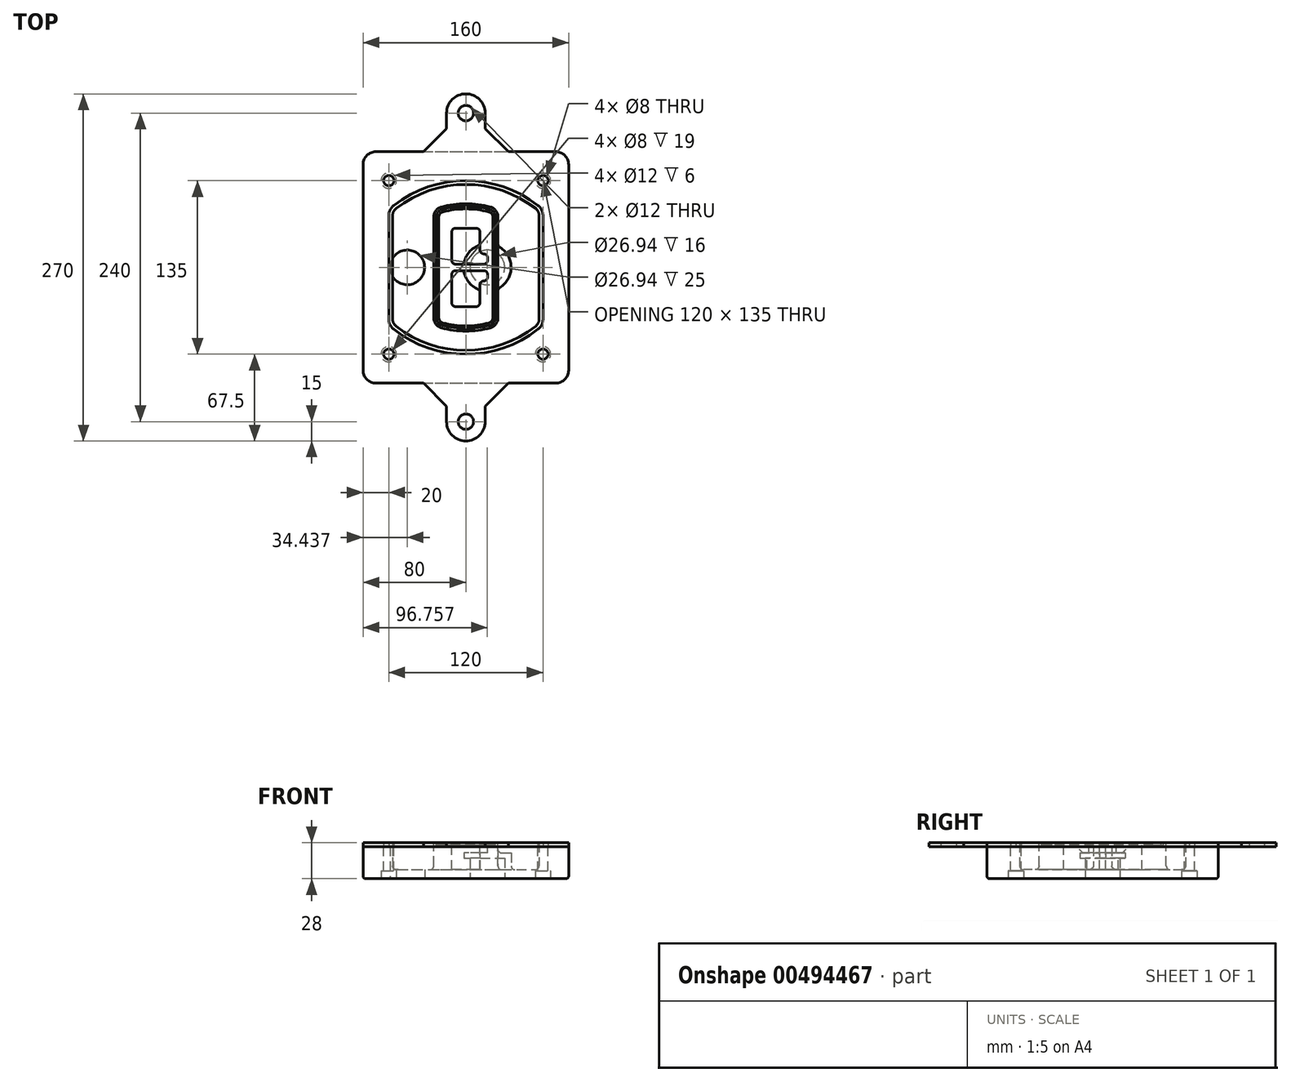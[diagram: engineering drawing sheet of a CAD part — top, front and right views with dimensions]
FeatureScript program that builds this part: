
annotation { "Feature Type Name" : "Feature", "Feature Type Description" : "" }
export const myFeature = defineFeature(function(context is Context, id is Id, definition is map)
    precondition{}
    {
        {
            var Q0;
            Q0=qCreatedBy(makeId("Top.planeOp"),FACE);
            var sketch = newSketch(context, id + "F0", { "sketchPlane" : qUnion([Q0])});
            skPoint(sketch, "E0.rect.middle", {"position": v(0, 0) * mm});
            skLineSegment(sketch, "E1.bottom", {"start": v(-70, -90) * mm, "end": v(70, -90) * mm});
            skLineSegment(sketch, "E1.top", {"start": v(-70, 90) * mm, "end": v(70, 90) * mm});
            skLineSegment(sketch, "E1.left", {"start": v(-80, -80) * mm, "end": v(-80, 80) * mm});
            skLineSegment(sketch, "E1.right", {"start": v(80, -80) * mm, "end": v(80, 80) * mm});
            skLineSegment(sketch, "E2", {"start": v(-80, 90) * mm, "end": v(80, -90) * mm, "construction": true});
            skLineSegment(sketch, "E3", {"start": v(80, 90) * mm, "end": v(-80, -90) * mm, "construction": true});
            skCircle(sketch, "E4", {"center": v(-60, 67.5) * mm, "radius": 4 * mm});
            skCircle(sketch, "E5", {"center": v(60, 67.5) * mm, "radius": 4 * mm});
            skCircle(sketch, "E6", {"center": v(60, -67.5) * mm, "radius": 4 * mm});
            skCircle(sketch, "E7", {"center": v(-60, -67.5) * mm, "radius": 4 * mm});
            skLineSegment(sketch, "E8", {"start": v(-60, 67.5) * mm, "end": v(60, 67.5) * mm, "construction": true});
            skLineSegment(sketch, "E9", {"start": v(60, 67.5) * mm, "end": v(60, -67.5) * mm, "construction": true});
            skLineSegment(sketch, "E10", {"start": v(60, -67.5) * mm, "end": v(-60, -67.5) * mm, "construction": true});
            skLineSegment(sketch, "E11", {"start": v(-60, -67.5) * mm, "end": v(-60, 67.5) * mm, "construction": true});
            skLineSegment(sketch, "E12", {"start": v(-60, 40.3) * mm, "end": v(-60, -40.3) * mm});
            skLineSegment(sketch, "E13", {"start": v(60, 40.3) * mm, "end": v(60, -40.3) * mm});
            skArc(sketch, "E14", {"start": v(56.15, 48.18) * mm, "mid": v(0, 67.5) * mm, "end": v(-56.15, 48.18) * mm});
            skArc(sketch, "E15", {"start": v(-56.15, -48.18) * mm, "mid": v(0, -67.5) * mm, "end": v(56.15, -48.18) * mm});
            skLineSegment(sketch, "E16", {"start": v(-60, 0) * mm, "end": v(60, 0) * mm, "construction": true});
            skPoint(sketch, "E17.visualSharp", {"position": v(-60, -45) * mm});
            skArc(sketch, "E17.filletArc", {"start": v(-60, -40.3) * mm, "mid": v(-58.99, -44.68) * mm, "end": v(-56.15, -48.18) * mm});
            skPoint(sketch, "E18.visualSharp", {"position": v(-60, 45) * mm});
            skArc(sketch, "E18.filletArc", {"start": v(-56.15, 48.18) * mm, "mid": v(-58.99, 44.68) * mm, "end": v(-60, 40.3) * mm});
            skPoint(sketch, "E19.visualSharp", {"position": v(60, 45) * mm});
            skArc(sketch, "E19.filletArc", {"start": v(60, 40.3) * mm, "mid": v(58.99, 44.68) * mm, "end": v(56.15, 48.18) * mm});
            skPoint(sketch, "E20.visualSharp", {"position": v(60, -45) * mm});
            skArc(sketch, "E20.filletArc", {"start": v(56.15, -48.18) * mm, "mid": v(58.99, -44.68) * mm, "end": v(60, -40.3) * mm});
            skPoint(sketch, "E21.visualSharp", {"position": v(-80, 90) * mm});
            skArc(sketch, "E21.filletArc", {"start": v(-70, 90) * mm, "mid": v(-77.07, 87.07) * mm, "end": v(-80, 80) * mm});
            skPoint(sketch, "E22.visualSharp", {"position": v(80, 90) * mm});
            skArc(sketch, "E22.filletArc", {"start": v(80, 80) * mm, "mid": v(77.07, 87.07) * mm, "end": v(70, 90) * mm});
            skPoint(sketch, "E23.visualSharp", {"position": v(80, -90) * mm});
            skArc(sketch, "E23.filletArc", {"start": v(70, -90) * mm, "mid": v(77.07, -87.07) * mm, "end": v(80, -80) * mm});
            skPoint(sketch, "E24.visualSharp", {"position": v(-80, -90) * mm});
            skArc(sketch, "E24.filletArc", {"start": v(-80, -80) * mm, "mid": v(-77.07, -87.07) * mm, "end": v(-70, -90) * mm});
            skArc(sketch, "E25.0", {"start": v(57, 40.3) * mm, "mid": v(56.3, 43.36) * mm, "end": v(54.3, 45.81) * mm});
            skLineSegment(sketch, "E25.1", {"start": v(57, 40.3) * mm, "end": v(57, -40.3) * mm});
            skArc(sketch, "E25.2", {"start": v(54.3, -45.81) * mm, "mid": v(56.3, -43.36) * mm, "end": v(57, -40.3) * mm});
            skArc(sketch, "E25.3", {"start": v(-54.3, -45.81) * mm, "mid": v(0, -64.5) * mm, "end": v(54.3, -45.81) * mm});
            skArc(sketch, "E25.4", {"start": v(-57, -40.3) * mm, "mid": v(-56.3, -43.36) * mm, "end": v(-54.3, -45.81) * mm});
            skArc(sketch, "E25.5", {"start": v(54.3, 45.81) * mm, "mid": v(0, 64.5) * mm, "end": v(-54.3, 45.81) * mm});
            skLineSegment(sketch, "E25.6", {"start": v(-57, 40.3) * mm, "end": v(-57, -40.3) * mm});
            skArc(sketch, "E25.7", {"start": v(-54.3, 45.81) * mm, "mid": v(-56.3, 43.36) * mm, "end": v(-57, 40.3) * mm});
            skArc(sketch, "E26.0", {"start": v(-58.62, 51.33) * mm, "mid": v(-62.58, 46.43) * mm, "end": v(-64, 40.3) * mm});
            skArc(sketch, "E26.1", {"start": v(58.62, 51.33) * mm, "mid": v(0, 71.5) * mm, "end": v(-58.62, 51.33) * mm});
            skArc(sketch, "E26.2", {"start": v(64, 40.3) * mm, "mid": v(62.58, 46.43) * mm, "end": v(58.62, 51.33) * mm});
            skLineSegment(sketch, "E26.3", {"start": v(64, 40.3) * mm, "end": v(64, -40.3) * mm});
            skArc(sketch, "E26.4", {"start": v(58.62, -51.33) * mm, "mid": v(62.58, -46.43) * mm, "end": v(64, -40.3) * mm});
            skLineSegment(sketch, "E26.5", {"start": v(-64, 40.3) * mm, "end": v(-64, -40.3) * mm});
            skArc(sketch, "E26.6", {"start": v(-58.62, -51.33) * mm, "mid": v(0, -71.5) * mm, "end": v(58.62, -51.33) * mm});
            skArc(sketch, "E26.7", {"start": v(-64, -40.3) * mm, "mid": v(-62.58, -46.43) * mm, "end": v(-58.62, -51.33) * mm});
            skSolve(sketch);
        }
        {
            var Q0;
            Q0=makeQuery(id+"F0.imprint","IMPRINT",FACE,{"disambiguationData":[TD([[makeQuery(id+"F0.imprint","IMPRINT",EDGE,{"derivedFrom":sQuery(id+"F0.wireOp",EDGE,"E1.bottom")}),1.0]])]});
            var Q1;
            Q1=makeQuery(id+"F0.imprint","IMPRINT",FACE,{"disambiguationData":[TD([[makeQuery(id+"F0.imprint","IMPRINT",EDGE,{"derivedFrom":sQuery(id+"F0.wireOp",EDGE,"E12")}),1.0]])]});
            var Q2;
            Q2=makeQuery(id+"F0.imprint","IMPRINT",FACE,{"disambiguationData":[TD([[makeQuery(id+"F0.imprint","IMPRINT",EDGE,{"derivedFrom":sQuery(id+"F0.wireOp",EDGE,"E25.0")}),1.0]])]});
            var Q3;
            Q3=makeQuery(id+"F0.imprint","IMPRINT",FACE,{"disambiguationData":[TD([[makeQuery(id+"F0.imprint","IMPRINT",EDGE,{"derivedFrom":sQuery(id+"F0.wireOp",EDGE,"E12")}),-1.0]])]});
            extrude(context, id + "F1", {"entities" : qUnion([Q0, Q1, Q2, Q3]), "oppositeDirection" : true, "depth" : 25 * mm});
        }
        {
            var Q0;
            Q0=makeQuery(id+"F0.imprint","IMPRINT",FACE,{"disambiguationData":[TD([[makeQuery(id+"F0.imprint","IMPRINT",EDGE,{"derivedFrom":sQuery(id+"F0.wireOp",EDGE,"E12")}),1.0]])]});
            extrude(context, id + "F2", {"entities" : qUnion([Q0]), "operationType" : NewBodyOperationType.ADD, "depth" : 3 * mm});
        }
        {
            var Q0;
            Q0=makeQuery(id+"F0.imprint","IMPRINT",FACE,{"disambiguationData":[TD([[makeQuery(id+"F0.imprint","IMPRINT",EDGE,{"derivedFrom":sQuery(id+"F0.wireOp",EDGE,"E25.0")}),1.0]])]});
            extrude(context, id + "F3", {"entities" : qUnion([Q0]), "operationType" : NewBodyOperationType.REMOVE, "oppositeDirection" : true, "depth" : 18 * mm});
        }
        {
            var Q0;
            Q0=makeQuery(id+"F2.opExtrude","CAP_FACE",FACE,{"disambiguationData":[OSD([sQuery(id+"F0.wireOp",EDGE,"E12"),sQuery(id+"F0.wireOp",EDGE,"E13"),sQuery(id+"F0.wireOp",EDGE,"E14"),sQuery(id+"F0.wireOp",EDGE,"E15"),sQuery(id+"F0.wireOp",EDGE,"E17.filletArc"),sQuery(id+"F0.wireOp",EDGE,"E18.filletArc"),sQuery(id+"F0.wireOp",EDGE,"E19.filletArc"),sQuery(id+"F0.wireOp",EDGE,"E20.filletArc"),sQuery(id+"F0.wireOp",EDGE,"E25.0"),sQuery(id+"F0.wireOp",EDGE,"E25.1"),sQuery(id+"F0.wireOp",EDGE,"E25.2"),sQuery(id+"F0.wireOp",EDGE,"E25.3"),sQuery(id+"F0.wireOp",EDGE,"E25.4"),sQuery(id+"F0.wireOp",EDGE,"E25.5"),sQuery(id+"F0.wireOp",EDGE,"E25.6"),sQuery(id+"F0.wireOp",EDGE,"E25.7")])],"isStart":false});
            var sketch = newSketch(context, id + "F4", { "sketchPlane" : qUnion([Q0])});
            skArc(sketch, "E27.0", {"start": v(-19.08, -46.97) * mm, "mid": v(0, -49.5) * mm, "end": v(19.08, -46.97) * mm});
            skArc(sketch, "E28.0", {"start": v(19.08, 46.97) * mm, "mid": v(0, 49.5) * mm, "end": v(-19.08, 46.97) * mm});
            skLineSegment(sketch, "E29", {"start": v(-25, 39.25) * mm, "end": v(-25, -39.25) * mm});
            skLineSegment(sketch, "E30", {"start": v(25, 39.25) * mm, "end": v(25, -39.25) * mm});
            skLineSegment(sketch, "E31", {"start": v(-25, 45.1) * mm, "end": v(25, 45.1) * mm, "construction": true});
            skLineSegment(sketch, "E32", {"start": v(-25, -45.1) * mm, "end": v(25, -45.1) * mm, "construction": true});
            skPoint(sketch, "E33.visualSharp", {"position": v(-25, 45.1) * mm});
            skArc(sketch, "E33.filletArc", {"start": v(-19.08, 46.97) * mm, "mid": v(-23.35, 44.11) * mm, "end": v(-25, 39.25) * mm});
            skPoint(sketch, "E34.visualSharp", {"position": v(25, 45.1) * mm});
            skArc(sketch, "E34.filletArc", {"start": v(25, 39.25) * mm, "mid": v(23.35, 44.11) * mm, "end": v(19.08, 46.97) * mm});
            skPoint(sketch, "E35.visualSharp", {"position": v(25, -45.1) * mm});
            skArc(sketch, "E35.filletArc", {"start": v(19.08, -46.97) * mm, "mid": v(23.35, -44.11) * mm, "end": v(25, -39.25) * mm});
            skPoint(sketch, "E36.visualSharp", {"position": v(-25, -45.1) * mm});
            skArc(sketch, "E36.filletArc", {"start": v(-25, -39.25) * mm, "mid": v(-23.35, -44.11) * mm, "end": v(-19.08, -46.97) * mm});
            skArc(sketch, "E37.0", {"start": v(54.3, 45.81) * mm, "mid": v(0, 64.5) * mm, "end": v(-54.3, 45.81) * mm});
            skArc(sketch, "E37.1", {"start": v(-54.3, 45.81) * mm, "mid": v(-56.3, 43.36) * mm, "end": v(-57, 40.3) * mm});
            skLineSegment(sketch, "E37.2", {"start": v(-57, 40.3) * mm, "end": v(-57, -40.3) * mm});
            skArc(sketch, "E37.3", {"start": v(-57, -40.3) * mm, "mid": v(-56.3, -43.36) * mm, "end": v(-54.3, -45.81) * mm});
            skArc(sketch, "E37.4", {"start": v(-54.3, -45.81) * mm, "mid": v(0, -64.5) * mm, "end": v(54.3, -45.81) * mm});
            skArc(sketch, "E37.5", {"start": v(54.3, -45.81) * mm, "mid": v(56.3, -43.36) * mm, "end": v(57, -40.3) * mm});
            skLineSegment(sketch, "E37.6", {"start": v(57, 40.3) * mm, "end": v(57, -40.3) * mm});
            skArc(sketch, "E37.7", {"start": v(57, 40.3) * mm, "mid": v(56.3, 43.36) * mm, "end": v(54.3, 45.81) * mm});
            skLineSegment(sketch, "E38.0", {"start": v(23, 39.25) * mm, "end": v(23, -39.25) * mm});
            skArc(sketch, "E38.1", {"start": v(18.56, -45.04) * mm, "mid": v(21.76, -42.9) * mm, "end": v(23, -39.25) * mm});
            skArc(sketch, "E38.2", {"start": v(-18.56, -45.04) * mm, "mid": v(0, -47.5) * mm, "end": v(18.56, -45.04) * mm});
            skArc(sketch, "E38.3", {"start": v(-23, -39.25) * mm, "mid": v(-21.76, -42.9) * mm, "end": v(-18.56, -45.04) * mm});
            skLineSegment(sketch, "E38.4", {"start": v(-23, 39.25) * mm, "end": v(-23, -39.25) * mm});
            skArc(sketch, "E38.5", {"start": v(23, 39.25) * mm, "mid": v(21.76, 42.9) * mm, "end": v(18.56, 45.04) * mm});
            skArc(sketch, "E38.6", {"start": v(-18.56, 45.04) * mm, "mid": v(-21.76, 42.9) * mm, "end": v(-23, 39.25) * mm});
            skArc(sketch, "E38.7", {"start": v(18.56, 45.04) * mm, "mid": v(0, 47.5) * mm, "end": v(-18.56, 45.04) * mm});
            skArc(sketch, "E39.0", {"start": v(21, 39.25) * mm, "mid": v(20.18, 41.68) * mm, "end": v(18.04, 43.1) * mm});
            skLineSegment(sketch, "E39.1", {"start": v(21, 39.25) * mm, "end": v(21, -39.25) * mm});
            skArc(sketch, "E39.2", {"start": v(18.04, -43.1) * mm, "mid": v(20.18, -41.68) * mm, "end": v(21, -39.25) * mm});
            skArc(sketch, "E39.3", {"start": v(-18.04, -43.1) * mm, "mid": v(0, -45.5) * mm, "end": v(18.04, -43.1) * mm});
            skArc(sketch, "E39.4", {"start": v(-21, -39.25) * mm, "mid": v(-20.18, -41.68) * mm, "end": v(-18.04, -43.1) * mm});
            skArc(sketch, "E39.5", {"start": v(18.04, 43.1) * mm, "mid": v(0, 45.5) * mm, "end": v(-18.04, 43.1) * mm});
            skLineSegment(sketch, "E39.6", {"start": v(-21, 39.25) * mm, "end": v(-21, -39.25) * mm});
            skArc(sketch, "E39.7", {"start": v(-18.04, 43.1) * mm, "mid": v(-20.18, 41.68) * mm, "end": v(-21, 39.25) * mm});
            skLineSegment(sketch, "E40", {"start": v(-25, 0) * mm, "end": v(25, 0) * mm, "construction": true});
            skLineSegment(sketch, "E41", {"start": v(-11, 5.5) * mm, "end": v(-11, 27.5) * mm});
            skLineSegment(sketch, "E42", {"start": v(-8, 30.5) * mm, "end": v(8, 30.5) * mm});
            skLineSegment(sketch, "E43", {"start": v(11, 27.5) * mm, "end": v(11, 13.5) * mm});
            skLineSegment(sketch, "E44", {"start": v(14, 10.5) * mm, "end": v(14, 10.5) * mm});
            skLineSegment(sketch, "E45", {"start": v(17, 7.5) * mm, "end": v(17, 5.5) * mm});
            skLineSegment(sketch, "E46", {"start": v(14, 2.5) * mm, "end": v(-8, 2.5) * mm});
            skPoint(sketch, "E47.visualSharp", {"position": v(-11, 30.5) * mm});
            skArc(sketch, "E47.filletArc", {"start": v(-8, 30.5) * mm, "mid": v(-10.12, 29.62) * mm, "end": v(-11, 27.5) * mm});
            skPoint(sketch, "E48.visualSharp", {"position": v(11, 30.5) * mm});
            skArc(sketch, "E48.filletArc", {"start": v(11, 27.5) * mm, "mid": v(10.12, 29.62) * mm, "end": v(8, 30.5) * mm});
            skPoint(sketch, "E49.visualSharp", {"position": v(11, 10.5) * mm});
            skArc(sketch, "E49.filletArc", {"start": v(11, 13.5) * mm, "mid": v(11.88, 11.38) * mm, "end": v(14, 10.5) * mm});
            skPoint(sketch, "E50.visualSharp", {"position": v(17, 10.5) * mm});
            skArc(sketch, "E50.filletArc", {"start": v(17, 7.5) * mm, "mid": v(16.12, 9.62) * mm, "end": v(14, 10.5) * mm});
            skPoint(sketch, "E51.visualSharp", {"position": v(17, 2.5) * mm});
            skArc(sketch, "E51.filletArc", {"start": v(14, 2.5) * mm, "mid": v(16.12, 3.38) * mm, "end": v(17, 5.5) * mm});
            skPoint(sketch, "E52.visualSharp", {"position": v(-11, 2.5) * mm});
            skArc(sketch, "E52.filletArc", {"start": v(-11, 5.5) * mm, "mid": v(-10.12, 3.38) * mm, "end": v(-8, 2.5) * mm});
            skLineSegment(sketch, "E53.0.MirrorCS", {"start": v(14, -2.5) * mm, "end": v(-8, -2.5) * mm});
            skArc(sketch, "E54.0.MirrorCS", {"start": v(-11, -5.5) * mm, "mid": v(-10.12, -3.38) * mm, "end": v(-8, -2.5) * mm});
            skLineSegment(sketch, "E55.0.MirrorCS", {"start": v(-11, -5.5) * mm, "end": v(-11, -27.5) * mm});
            skArc(sketch, "E56.0.MirrorCS", {"start": v(-8, -30.5) * mm, "mid": v(-10.12, -29.62) * mm, "end": v(-11, -27.5) * mm});
            skLineSegment(sketch, "E57.0.MirrorCS", {"start": v(-8, -30.5) * mm, "end": v(8, -30.5) * mm});
            skArc(sketch, "E58.0.MirrorCS", {"start": v(11, -27.5) * mm, "mid": v(10.12, -29.62) * mm, "end": v(8, -30.5) * mm});
            skLineSegment(sketch, "E59.0.MirrorCS", {"start": v(11, -27.5) * mm, "end": v(11, -13.5) * mm});
            skArc(sketch, "E60.0.MirrorCS", {"start": v(11, -13.5) * mm, "mid": v(11.88, -11.38) * mm, "end": v(14, -10.5) * mm});
            skArc(sketch, "E61.0.MirrorCS", {"start": v(17, -7.5) * mm, "mid": v(16.12, -9.62) * mm, "end": v(14, -10.5) * mm});
            skLineSegment(sketch, "E62.0.MirrorCS", {"start": v(17, -7.5) * mm, "end": v(17, -5.5) * mm});
            skArc(sketch, "E63.0.MirrorCS", {"start": v(14, -2.5) * mm, "mid": v(16.12, -3.38) * mm, "end": v(17, -5.5) * mm});
            skSolve(sketch);
        }
        {
            var Q0;
            Q0=makeQuery(id+"F4.imprint","IMPRINT",FACE,{"disambiguationData":[TD([[makeQuery(id+"F4.imprint","IMPRINT",EDGE,{"derivedFrom":sQuery(id+"F4.wireOp",EDGE,"E27.0")}),1.0]])]});
            var Q1;
            Q1=makeQuery(id+"F4.imprint","IMPRINT",FACE,{"disambiguationData":[TD([[makeQuery(id+"F4.imprint","IMPRINT",EDGE,{"derivedFrom":sQuery(id+"F4.wireOp",EDGE,"E38.0")}),-1.0]])]});
            var Q2;
            Q2=makeQuery(id+"F4.imprint","IMPRINT",FACE,{"disambiguationData":[TD([[makeQuery(id+"F4.imprint","IMPRINT",EDGE,{"derivedFrom":sQuery(id+"F4.wireOp",EDGE,"E39.0")}),1.0]])]});
            extrude(context, id + "F5", {"entities" : qUnion([Q0, Q1, Q2]), "operationType" : NewBodyOperationType.ADD, "endBound" : BoundingType.UP_TO_NEXT, "oppositeDirection" : true, "depth" : 25 * mm});
        }
        {
            var Q0;
            Q0=makeQuery(id+"F4.imprint","IMPRINT",FACE,{"disambiguationData":[TD([[makeQuery(id+"F4.imprint","IMPRINT",EDGE,{"derivedFrom":sQuery(id+"F4.wireOp",EDGE,"E38.0")}),-1.0]])]});
            extrude(context, id + "F6", {"entities" : qUnion([Q0]), "operationType" : NewBodyOperationType.REMOVE, "oppositeDirection" : true, "depth" : 2 * mm});
        }
        {
            var Q0;
            Q0=makeQuery(id+"F1.opExtrude","CAP_FACE",FACE,{"disambiguationData":[OSD([sQuery(id+"F0.wireOp",EDGE,"E1.bottom"),sQuery(id+"F0.wireOp",EDGE,"E1.top"),sQuery(id+"F0.wireOp",EDGE,"E1.left"),sQuery(id+"F0.wireOp",EDGE,"E1.right"),sQuery(id+"F0.wireOp",EDGE,"E4"),sQuery(id+"F0.wireOp",EDGE,"E5"),sQuery(id+"F0.wireOp",EDGE,"E6"),sQuery(id+"F0.wireOp",EDGE,"E7"),sQuery(id+"F0.wireOp",EDGE,"E21.filletArc"),sQuery(id+"F0.wireOp",EDGE,"E22.filletArc"),sQuery(id+"F0.wireOp",EDGE,"E23.filletArc"),sQuery(id+"F0.wireOp",EDGE,"E24.filletArc")])],"isStart":false});
            var sketch = newSketch(context, id + "F7", { "sketchPlane" : qUnion([Q0])});
            skCircle(sketch, "E64", {"center": v(16.76, 0) * mm, "radius": 13.47 * mm});
            skCircle(sketch, "E65", {"center": v(-45.56, 0) * mm, "radius": 13.47 * mm});
            skLineSegment(sketch, "E66", {"start": v(80, 0) * mm, "end": v(-80, 0) * mm});
            skCircle(sketch, "E67", {"center": v(16.76, 0) * mm, "radius": 18.47 * mm});
            skCircle(sketch, "E68", {"center": v(60, -67.5) * mm, "radius": 6 * mm});
            skCircle(sketch, "E69", {"center": v(-60, -67.5) * mm, "radius": 6 * mm});
            skCircle(sketch, "E70", {"center": v(-60, 67.5) * mm, "radius": 6 * mm});
            skCircle(sketch, "E71", {"center": v(60, 67.5) * mm, "radius": 6 * mm});
            skSolve(sketch);
        }
        {
            var Q0;
            {var subQ1=sQuery(id+"F7.wireOp",EDGE,"E66");var subQ4=sQuery(id+"F7.wireOp",EDGE,"E64");var subQ6=makeQuery(id+"F7.imprint","INTERSECT",VERTEX,{"disambiguationData":[OD(0.0)],"derivedFrom":[subQ4,subQ1]});Q0=makeQuery(id+"F7.imprint","IMPRINT",FACE,{"disambiguationData":[TD([[makeQuery(id+"F7.imprint","IMPRINT",EDGE,{"disambiguationData":[TD([[subQ6,-1.0]])],"derivedFrom":subQ4}),-1.0]])]});}
            var Q1;
            {var subQ0=sQuery(id+"F7.wireOp",EDGE,"E66");var subQ1=sQuery(id+"F7.wireOp",EDGE,"E64");var subQ3=makeQuery(id+"F7.imprint","INTERSECT",VERTEX,{"disambiguationData":[OD(0.0)],"derivedFrom":[subQ1,subQ0]});Q1=makeQuery(id+"F7.imprint","IMPRINT",FACE,{"disambiguationData":[TD([[makeQuery(id+"F7.imprint","IMPRINT",EDGE,{"disambiguationData":[TD([[subQ3,-1.0]])],"derivedFrom":subQ1}),1.0]])]});}
            var Q2;
            {var subQ0=sQuery(id+"F7.wireOp",EDGE,"E66");var subQ1=sQuery(id+"F7.wireOp",EDGE,"E64");var subQ3=makeQuery(id+"F7.imprint","INTERSECT",VERTEX,{"disambiguationData":[OD(0.0)],"derivedFrom":[subQ1,subQ0]});Q2=makeQuery(id+"F7.imprint","IMPRINT",FACE,{"disambiguationData":[TD([[makeQuery(id+"F7.imprint","IMPRINT",EDGE,{"disambiguationData":[TD([[subQ3,1.0]])],"derivedFrom":subQ1}),1.0]])]});}
            var Q3;
            {var subQ1=sQuery(id+"F7.wireOp",EDGE,"E66");var subQ4=sQuery(id+"F7.wireOp",EDGE,"E64");var subQ6=makeQuery(id+"F7.imprint","INTERSECT",VERTEX,{"disambiguationData":[OD(0.0)],"derivedFrom":[subQ4,subQ1]});Q3=makeQuery(id+"F7.imprint","IMPRINT",FACE,{"disambiguationData":[TD([[makeQuery(id+"F7.imprint","IMPRINT",EDGE,{"disambiguationData":[TD([[subQ6,1.0]])],"derivedFrom":subQ4}),-1.0]])]});}
            extrude(context, id + "F8", {"entities" : qUnion([Q0, Q1, Q2, Q3]), "operationType" : NewBodyOperationType.ADD, "oppositeDirection" : true, "depth" : 20 * mm});
        }
        {
            var Q0;
            {var subQ0=sQuery(id+"F7.wireOp",EDGE,"E66");var subQ1=sQuery(id+"F7.wireOp",EDGE,"E64");var subQ3=makeQuery(id+"F7.imprint","INTERSECT",VERTEX,{"disambiguationData":[OD(0.0)],"derivedFrom":[subQ1,subQ0]});Q0=makeQuery(id+"F7.imprint","IMPRINT",FACE,{"disambiguationData":[TD([[makeQuery(id+"F7.imprint","IMPRINT",EDGE,{"disambiguationData":[TD([[subQ3,-1.0]])],"derivedFrom":subQ1}),1.0]])]});}
            var Q1;
            {var subQ0=sQuery(id+"F7.wireOp",EDGE,"E66");var subQ1=sQuery(id+"F7.wireOp",EDGE,"E64");var subQ3=makeQuery(id+"F7.imprint","INTERSECT",VERTEX,{"disambiguationData":[OD(0.0)],"derivedFrom":[subQ1,subQ0]});Q1=makeQuery(id+"F7.imprint","IMPRINT",FACE,{"disambiguationData":[TD([[makeQuery(id+"F7.imprint","IMPRINT",EDGE,{"disambiguationData":[TD([[subQ3,1.0]])],"derivedFrom":subQ1}),1.0]])]});}
            extrude(context, id + "F9", {"entities" : qUnion([Q0, Q1]), "operationType" : NewBodyOperationType.REMOVE, "oppositeDirection" : true, "depth" : 16 * mm});
        }
        {
            var Q0;
            {var subQ0=sQuery(id+"F7.wireOp",EDGE,"E66");var subQ1=sQuery(id+"F7.wireOp",EDGE,"E65");var subQ3=makeQuery(id+"F7.imprint","INTERSECT",VERTEX,{"disambiguationData":[OD(0.0)],"derivedFrom":[subQ1,subQ0]});Q0=makeQuery(id+"F7.imprint","IMPRINT",FACE,{"disambiguationData":[TD([[makeQuery(id+"F7.imprint","IMPRINT",EDGE,{"disambiguationData":[TD([[subQ3,-1.0]])],"derivedFrom":subQ1}),1.0]])]});}
            var Q1;
            {var subQ0=sQuery(id+"F7.wireOp",EDGE,"E66");var subQ1=sQuery(id+"F7.wireOp",EDGE,"E65");var subQ3=makeQuery(id+"F7.imprint","INTERSECT",VERTEX,{"disambiguationData":[OD(0.0)],"derivedFrom":[subQ1,subQ0]});Q1=makeQuery(id+"F7.imprint","IMPRINT",FACE,{"disambiguationData":[TD([[makeQuery(id+"F7.imprint","IMPRINT",EDGE,{"disambiguationData":[TD([[subQ3,1.0]])],"derivedFrom":subQ1}),1.0]])]});}
            extrude(context, id + "F10", {"entities" : qUnion([Q0, Q1]), "operationType" : NewBodyOperationType.REMOVE, "oppositeDirection" : true, "depth" : 25 * mm});
        }
        {
            var Q0;
            Q0=makeQuery(id+"F7.imprint","IMPRINT",FACE,{"disambiguationData":[TD([[makeQuery(id+"F7.imprint","IMPRINT",EDGE,{"derivedFrom":sQuery(id+"F7.wireOp",EDGE,"E68")}),1.0]])]});
            var Q1;
            Q1=makeQuery(id+"F7.imprint","IMPRINT",FACE,{"disambiguationData":[TD([[makeQuery(id+"F7.imprint","IMPRINT",EDGE,{"derivedFrom":makeQuery(id+"F1.opExtrude","CAP_EDGE",EDGE,{"disambiguationData":[OSD([sQuery(id+"F0.wireOp",EDGE,"E5")])],"isStart":false})}),-1.0]])]});
            var Q2;
            Q2=makeQuery(id+"F7.imprint","IMPRINT",FACE,{"disambiguationData":[TD([[makeQuery(id+"F7.imprint","IMPRINT",EDGE,{"derivedFrom":sQuery(id+"F7.wireOp",EDGE,"E69")}),1.0]])]});
            var Q3;
            Q3=makeQuery(id+"F7.imprint","IMPRINT",FACE,{"disambiguationData":[TD([[makeQuery(id+"F7.imprint","IMPRINT",EDGE,{"derivedFrom":makeQuery(id+"F1.opExtrude","CAP_EDGE",EDGE,{"disambiguationData":[OSD([sQuery(id+"F0.wireOp",EDGE,"E4")])],"isStart":false})}),-1.0]])]});
            var Q4;
            Q4=makeQuery(id+"F7.imprint","IMPRINT",FACE,{"disambiguationData":[TD([[makeQuery(id+"F7.imprint","IMPRINT",EDGE,{"derivedFrom":sQuery(id+"F7.wireOp",EDGE,"E70")}),1.0]])]});
            var Q5;
            Q5=makeQuery(id+"F7.imprint","IMPRINT",FACE,{"disambiguationData":[TD([[makeQuery(id+"F7.imprint","IMPRINT",EDGE,{"derivedFrom":makeQuery(id+"F1.opExtrude","CAP_EDGE",EDGE,{"disambiguationData":[OSD([sQuery(id+"F0.wireOp",EDGE,"E7")])],"isStart":false})}),-1.0]])]});
            var Q6;
            Q6=makeQuery(id+"F7.imprint","IMPRINT",FACE,{"disambiguationData":[TD([[makeQuery(id+"F7.imprint","IMPRINT",EDGE,{"derivedFrom":sQuery(id+"F7.wireOp",EDGE,"E71")}),1.0]])]});
            var Q7;
            Q7=makeQuery(id+"F7.imprint","IMPRINT",FACE,{"disambiguationData":[TD([[makeQuery(id+"F7.imprint","IMPRINT",EDGE,{"derivedFrom":makeQuery(id+"F1.opExtrude","CAP_EDGE",EDGE,{"disambiguationData":[OSD([sQuery(id+"F0.wireOp",EDGE,"E6")])],"isStart":false})}),-1.0]])]});
            extrude(context, id + "F11", {"entities" : qUnion([Q0, Q1, Q2, Q3, Q4, Q5, Q6, Q7]), "operationType" : NewBodyOperationType.REMOVE, "oppositeDirection" : true, "depth" : 6 * mm});
        }
        {
            var Q0;
            Q0=makeQuery(id+"F9.boolean.opBoolean","COPY",FACE,{"derivedFrom":makeQuery(id+"F9.opExtrude","CAP_FACE",FACE,{"disambiguationData":[OSD([sQuery(id+"F7.wireOp",EDGE,"E64")])],"isStart":false})});
            var sketch = newSketch(context, id + "F12", { "sketchPlane" : qUnion([Q0])});
            skArc(sketch, "E72.0", {"start": v(11, 17.55) * mm, "mid": v(2.57, 11.82) * mm, "end": v(-1.54, 2.5) * mm});
            skArc(sketch, "E72.1", {"start": v(-1.54, -2.5) * mm, "mid": v(2.57, -11.82) * mm, "end": v(11, -17.55) * mm});
            skLineSegment(sketch, "E73", {"start": v(-1.54, -2.5) * mm, "end": v(14, -2.5) * mm});
            skLineSegment(sketch, "E74.0", {"start": v(14, 2.5) * mm, "end": v(-1.54, 2.5) * mm});
            skArc(sketch, "E74.1", {"start": v(14, 2.5) * mm, "mid": v(16.12, 3.38) * mm, "end": v(17, 5.5) * mm});
            skLineSegment(sketch, "E74.2", {"start": v(17, 7.5) * mm, "end": v(17, 5.5) * mm});
            skArc(sketch, "E74.3", {"start": v(17, 7.5) * mm, "mid": v(16.12, 9.62) * mm, "end": v(14, 10.5) * mm});
            skArc(sketch, "E74.4", {"start": v(11, 13.5) * mm, "mid": v(11.88, 11.38) * mm, "end": v(14, 10.5) * mm});
            skLineSegment(sketch, "E74.5", {"start": v(11, 17.55) * mm, "end": v(11, 13.5) * mm});
            skLineSegment(sketch, "E74.7", {"start": v(14, -2.5) * mm, "end": v(-1.54, -2.5) * mm});
            skArc(sketch, "E74.8", {"start": v(14, -2.5) * mm, "mid": v(16.12, -3.38) * mm, "end": v(17, -5.5) * mm});
            skLineSegment(sketch, "E74.9", {"start": v(17, -7.5) * mm, "end": v(17, -5.5) * mm});
            skArc(sketch, "E74.10", {"start": v(17, -7.5) * mm, "mid": v(16.12, -9.62) * mm, "end": v(14, -10.5) * mm});
            skArc(sketch, "E74.11", {"start": v(11, -13.5) * mm, "mid": v(11.88, -11.38) * mm, "end": v(14, -10.5) * mm});
            skLineSegment(sketch, "E74.12", {"start": v(11, -17.55) * mm, "end": v(11, -13.5) * mm});
            skPoint(sketch, "E75.orphan", {"position": v(11, -27.5) * mm});
            skPoint(sketch, "E76.orphan", {"position": v(-8, -2.5) * mm});
            skPoint(sketch, "E77.orphan", {"position": v(-8, 2.5) * mm});
            skPoint(sketch, "E78.orphan", {"position": v(11, 27.5) * mm});
            skSolve(sketch);
        }
        {
            var Q0;
            {var subQ7=sQuery(id+"F12.wireOp",EDGE,"E72.0");var subQ14=sQuery(id+"F12.wireOp",EDGE,"E72.1");var subQ16=sQuery(id+"F12.wireOp",EDGE,"E74.1");var subQ18=sQuery(id+"F12.wireOp",EDGE,"E74.8");Q0=qUnion([makeQuery(id+"F12.imprint","IMPRINT",FACE,{"disambiguationData":[TD([[makeQuery(id+"F12.imprint","IMPRINT",EDGE,{"derivedFrom":subQ7}),1.0]])]}),makeQuery(id+"F12.imprint","IMPRINT",FACE,{"disambiguationData":[TD([[makeQuery(id+"F12.imprint","IMPRINT",EDGE,{"derivedFrom":subQ14}),1.0]])]}),makeQuery(id+"F12.imprint","IMPRINT",FACE,{"disambiguationData":[TD([[makeQuery(id+"F12.imprint","IMPRINT",EDGE,{"derivedFrom":subQ16}),1.0]])]}),makeQuery(id+"F12.imprint","IMPRINT",FACE,{"disambiguationData":[TD([[makeQuery(id+"F12.imprint","IMPRINT",EDGE,{"derivedFrom":subQ18}),-1.0]])]})]);}
            var Q1;
            Q1=makeQuery(id+"F5.boolean.opBoolean","SPLIT",FACE,{"disambiguationData":[TD([makeQuery(id+"F5.opExtrude","SWEPT_FACE",FACE,{"disambiguationData":[OSD([sQuery(id+"F4.wireOp",EDGE,"E41")])]})])],"derivedFrom":makeQuery(id+"F3.boolean.opBoolean","COPY",FACE,{"derivedFrom":makeQuery(id+"F3.opExtrude","CAP_FACE",FACE,{"disambiguationData":[OSD([sQuery(id+"F0.wireOp",EDGE,"E25.0"),sQuery(id+"F0.wireOp",EDGE,"E25.1"),sQuery(id+"F0.wireOp",EDGE,"E25.2"),sQuery(id+"F0.wireOp",EDGE,"E25.3"),sQuery(id+"F0.wireOp",EDGE,"E25.4"),sQuery(id+"F0.wireOp",EDGE,"E25.5"),sQuery(id+"F0.wireOp",EDGE,"E25.6"),sQuery(id+"F0.wireOp",EDGE,"E25.7")])],"isStart":false})})});
            extrude(context, id + "F13", {"entities" : qUnion([Q0]), "operationType" : NewBodyOperationType.REMOVE, "endBound" : BoundingType.UP_TO_SURFACE, "endBoundEntityFace" : qUnion([Q1]), "depth" : 25 * mm});
        }
        {
            var Q0;
            Q0=makeQuery(id+"F3.boolean.opBoolean","COPY",EDGE,{"derivedFrom":makeQuery(id+"F3.opExtrude","CAP_EDGE",EDGE,{"disambiguationData":[OSD([sQuery(id+"F0.wireOp",EDGE,"E25.6")])],"isStart":false})});
            var Q1;
            Q1=makeQuery(id+"F8.boolean.opBoolean","INTERSECT",EDGE,{"derivedFrom":[makeQuery(id+"F5.opExtrude","SWEPT_FACE",FACE,{"disambiguationData":[OSD([sQuery(id+"F4.wireOp",EDGE,"E30")])]}),makeQuery(id+"F8.opExtrude","CAP_FACE",FACE,{"disambiguationData":[OSD([sQuery(id+"F7.wireOp",EDGE,"E67")])],"isStart":false})]});
            var Q2;
            Q2=makeQuery(id+"F8.boolean.opBoolean","INTERSECT",EDGE,{"disambiguationData":[OD(1.0)],"derivedFrom":[makeQuery(id+"F5.opExtrude","SWEPT_FACE",FACE,{"disambiguationData":[OSD([sQuery(id+"F4.wireOp",EDGE,"E30")])]}),makeQuery(id+"F8.opExtrude","SWEPT_FACE",FACE,{"disambiguationData":[OSD([sQuery(id+"F7.wireOp",EDGE,"E67")])]})]});
            var Q3;
            {var subQ0=sQuery(id+"F4.wireOp",EDGE,"E30");Q3=makeQuery(id+"F8.boolean.opBoolean","SPLIT",EDGE,{"disambiguationData":[TD([makeQuery(id+"F5.opExtrude","SWEPT_FACE",FACE,{"disambiguationData":[OSD([sQuery(id+"F4.wireOp",EDGE,"E35.filletArc")])]})])],"derivedFrom":makeQuery(id+"F5.opExtrude","CAP_EDGE",EDGE,{"disambiguationData":[OSD([subQ0])],"isStart":false})});}
            var Q4;
            {var subQ0=sQuery(id+"F0.wireOp",EDGE,"E25.7");var subQ1=sQuery(id+"F0.wireOp",EDGE,"E25.1");var subQ2=sQuery(id+"F0.wireOp",EDGE,"E25.6");var subQ3=sQuery(id+"F0.wireOp",EDGE,"E25.5");var subQ4=sQuery(id+"F0.wireOp",EDGE,"E25.4");var subQ5=sQuery(id+"F0.wireOp",EDGE,"E25.0");var subQ6=sQuery(id+"F0.wireOp",EDGE,"E25.2");var subQ7=sQuery(id+"F0.wireOp",EDGE,"E25.3");Q4=makeQuery(id+"F8.boolean.opBoolean","INTERSECT",EDGE,{"derivedFrom":[makeQuery(id+"F5.boolean.opBoolean","SPLIT",FACE,{"disambiguationData":[TD([makeQuery(id+"F2.opExtrude","SWEPT_FACE",FACE,{"disambiguationData":[OSD([subQ5])]})])],"derivedFrom":makeQuery(id+"F3.boolean.opBoolean","COPY",FACE,{"derivedFrom":makeQuery(id+"F3.opExtrude","CAP_FACE",FACE,{"disambiguationData":[OSD([subQ5,subQ1,subQ6,subQ7,subQ4,subQ3,subQ2,subQ0])],"isStart":false})})}),makeQuery(id+"F8.opExtrude","SWEPT_FACE",FACE,{"disambiguationData":[OSD([sQuery(id+"F7.wireOp",EDGE,"E67")])]})]});}
            var Q5;
            Q5=makeQuery(id+"F8.boolean.opBoolean","INTERSECT",EDGE,{"disambiguationData":[OD(0.0)],"derivedFrom":[makeQuery(id+"F5.opExtrude","SWEPT_FACE",FACE,{"disambiguationData":[OSD([sQuery(id+"F4.wireOp",EDGE,"E30")])]}),makeQuery(id+"F8.opExtrude","SWEPT_FACE",FACE,{"disambiguationData":[OSD([sQuery(id+"F7.wireOp",EDGE,"E67")])]})]});
            fillet(context, id + "F14", {"entities" : qUnion([Q0, Q1, Q2, Q3, Q4, Q5]), "radius" : 3 * mm, "tangentPropagation" : true, "allowEdgeOverflow" : false});
        }
        {
            var Q0;
            Q0=makeQuery(id+"F1.opExtrude","CAP_EDGE",EDGE,{"disambiguationData":[OSD([sQuery(id+"F0.wireOp",EDGE,"E1.bottom")])],"isStart":false});
            fillet(context, id + "F15", {"entities" : qUnion([Q0]), "radius" : 2 * mm, "tangentPropagation" : true, "allowEdgeOverflow" : false});
        }
        {
            var Q0;
            {var subQ0=sQuery(id+"F0.wireOp",EDGE,"E21.filletArc");var subQ1=sQuery(id+"F0.wireOp",EDGE,"E7");var subQ2=sQuery(id+"F0.wireOp",EDGE,"E6");var subQ3=sQuery(id+"F0.wireOp",EDGE,"E5");var subQ4=sQuery(id+"F0.wireOp",EDGE,"E4");var subQ5=sQuery(id+"F0.wireOp",EDGE,"E22.filletArc");var subQ6=sQuery(id+"F0.wireOp",EDGE,"E1.bottom");var subQ7=sQuery(id+"F0.wireOp",EDGE,"E1.right");var subQ8=sQuery(id+"F0.wireOp",EDGE,"E1.top");var subQ9=sQuery(id+"F0.wireOp",EDGE,"E1.left");var subQ10=sQuery(id+"F0.wireOp",EDGE,"E23.filletArc");var subQ11=sQuery(id+"F0.wireOp",EDGE,"E24.filletArc");Q0=makeQuery(id+"F2.boolean.opBoolean","SPLIT",FACE,{"disambiguationData":[TD([makeQuery(id+"F1.opExtrude","SWEPT_FACE",FACE,{"disambiguationData":[OSD([subQ6])]})])],"derivedFrom":makeQuery(id+"F1.opExtrude","CAP_FACE",FACE,{"disambiguationData":[OSD([subQ6,subQ8,subQ9,subQ7,subQ4,subQ3,subQ2,subQ1,subQ0,subQ5,subQ10,subQ11])],"isStart":true})});}
            var sketch = newSketch(context, id + "F16", { "sketchPlane" : qUnion([Q0])});
            skLineSegment(sketch, "E79", {"start": v(0, 90) * mm, "end": v(0, 120) * mm, "construction": true});
            skLineSegment(sketch, "E80", {"start": v(0, 90) * mm, "end": v(-33, 90) * mm});
            skLineSegment(sketch, "E81", {"start": v(0, 90) * mm, "end": v(33, 90) * mm});
            skLineSegment(sketch, "E82", {"start": v(-33, 90) * mm, "end": v(-15, 108) * mm});
            skLineSegment(sketch, "E83", {"start": v(33, 90) * mm, "end": v(15, 108) * mm});
            skLineSegment(sketch, "E84", {"start": v(-15, 108) * mm, "end": v(-15, 120) * mm});
            skLineSegment(sketch, "E85", {"start": v(15, 108) * mm, "end": v(15, 120) * mm});
            skArc(sketch, "E86", {"start": v(15, 120) * mm, "mid": v(0, 135) * mm, "end": v(-15, 120) * mm});
            skCircle(sketch, "E87", {"center": v(0, 120) * mm, "radius": 6 * mm});
            skLineSegment(sketch, "E88", {"start": v(-80, 0) * mm, "end": v(80, 0) * mm, "construction": true});
            skLineSegment(sketch, "E89.MirrorCS", {"start": v(0, -90) * mm, "end": v(0, -120) * mm, "construction": true});
            skLineSegment(sketch, "E90.MirrorCS", {"start": v(0, -90) * mm, "end": v(33, -90) * mm});
            skLineSegment(sketch, "E91.MirrorCS", {"start": v(-33, -90) * mm, "end": v(-15, -108) * mm});
            skArc(sketch, "E92.MirrorCS", {"start": v(15, -120) * mm, "mid": v(0, -135) * mm, "end": v(-15, -120) * mm});
            skLineSegment(sketch, "E93.MirrorCS", {"start": v(-15, -108) * mm, "end": v(-15, -120) * mm});
            skCircle(sketch, "E94.MirrorC", {"center": v(0, -120) * mm, "radius": 6 * mm});
            skLineSegment(sketch, "E95.MirrorCS", {"start": v(0, -90) * mm, "end": v(-33, -90) * mm});
            skLineSegment(sketch, "E96.MirrorCS", {"start": v(15, -108) * mm, "end": v(15, -120) * mm});
            skLineSegment(sketch, "E97.MirrorCS", {"start": v(33, -90) * mm, "end": v(15, -108) * mm});
            skSolve(sketch);
        }
        {
            var Q0;
            Q0=makeQuery(id+"F16.imprint","IMPRINT",FACE,{"disambiguationData":[TD([[makeQuery(id+"F16.imprint","IMPRINT",EDGE,{"derivedFrom":sQuery(id+"F16.wireOp",EDGE,"E90.MirrorCS")}),-1.0]])]});
            var Q1;
            Q1=makeQuery(id+"F16.imprint","IMPRINT",FACE,{"disambiguationData":[TD([[makeQuery(id+"F16.imprint","IMPRINT",EDGE,{"derivedFrom":sQuery(id+"F16.wireOp",EDGE,"E80")}),1.0]])]});
            var Q2;
            {var subQ7=sQuery(id+"F16.wireOp",EDGE,"E80");Q2=makeQuery(id+"F16.imprint","IMPRINT",FACE,{"disambiguationData":[TD([[makeQuery(id+"F16.imprint","IMPRINT",EDGE,{"derivedFrom":subQ7}),-1.0]])]});}
            var Q3;
            Q3=makeQuery(id+"F2.opExtrude","CAP_FACE",FACE,{"disambiguationData":[OSD([sQuery(id+"F0.wireOp",EDGE,"E12"),sQuery(id+"F0.wireOp",EDGE,"E13"),sQuery(id+"F0.wireOp",EDGE,"E14"),sQuery(id+"F0.wireOp",EDGE,"E15"),sQuery(id+"F0.wireOp",EDGE,"E17.filletArc"),sQuery(id+"F0.wireOp",EDGE,"E18.filletArc"),sQuery(id+"F0.wireOp",EDGE,"E19.filletArc"),sQuery(id+"F0.wireOp",EDGE,"E20.filletArc"),sQuery(id+"F0.wireOp",EDGE,"E25.0"),sQuery(id+"F0.wireOp",EDGE,"E25.1"),sQuery(id+"F0.wireOp",EDGE,"E25.2"),sQuery(id+"F0.wireOp",EDGE,"E25.3"),sQuery(id+"F0.wireOp",EDGE,"E25.4"),sQuery(id+"F0.wireOp",EDGE,"E25.5"),sQuery(id+"F0.wireOp",EDGE,"E25.6"),sQuery(id+"F0.wireOp",EDGE,"E25.7")])],"isStart":false});
            extrude(context, id + "F17", {"entities" : qUnion([Q0, Q1, Q2]), "endBound" : BoundingType.UP_TO_SURFACE, "endBoundEntityFace" : qUnion([Q3]), "depth" : 25 * mm});
        }
    });
